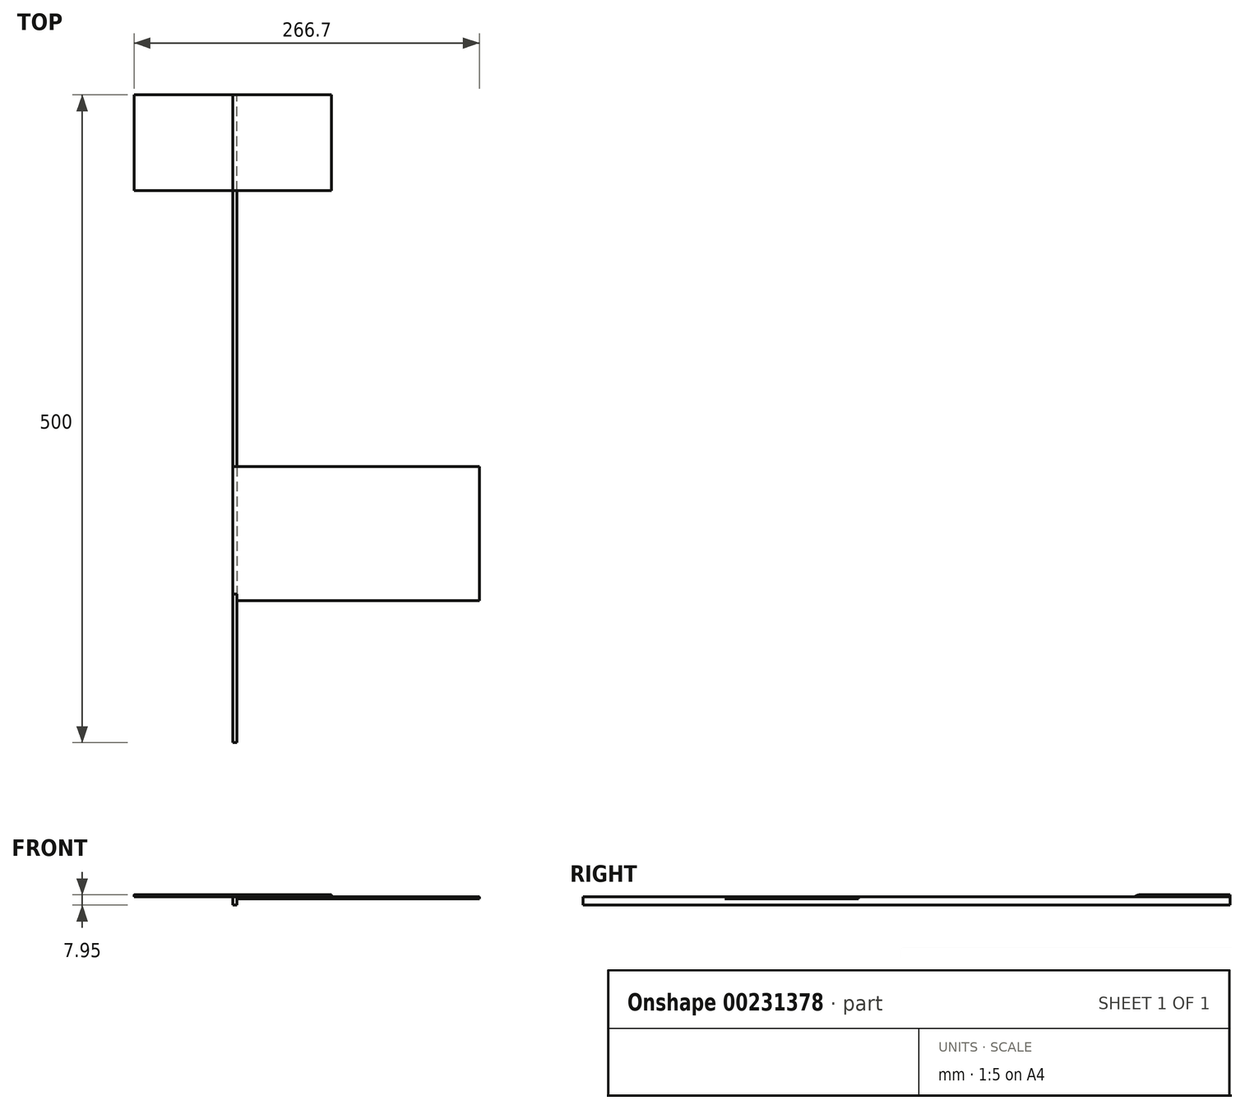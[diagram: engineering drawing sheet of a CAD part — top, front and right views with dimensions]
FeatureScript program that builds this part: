
annotation { "Feature Type Name" : "Feature", "Feature Type Description" : "" }
export const myFeature = defineFeature(function(context is Context, id is Id, definition is map)
    precondition{}
    {
        {
            var Q0;
            Q0=qCreatedBy(makeId("Front.planeOp"),FACE);
            var sketch = newSketch(context, id + "F0", { "sketchPlane" : qUnion([Q0])});
            skLineSegment(sketch, "E0.bottom", {"start": v(0, 0) * mm, "end": v(3.18, 0) * mm});
            skLineSegment(sketch, "E0.top", {"start": v(0, 6.35) * mm, "end": v(3.17, 6.35) * mm});
            skLineSegment(sketch, "E0.left", {"start": v(0, 0) * mm, "end": v(0, 6.35) * mm});
            skLineSegment(sketch, "E0.right", {"start": v(3.18, 0) * mm, "end": v(3.17, 6.35) * mm});
            skSolve(sketch);
        }
        {
            var Q0;
            Q0 = qSketchRegion(id + "F0", true);
            extrude(context, id + "F1", {"entities" : qUnion([Q0]), "depth" : 500 * mm});
        }
        {
            var Q0;
            Q0=qCreatedBy(makeId("Right.planeOp"),FACE);
            var sketch = newSketch(context, id + "F2", { "sketchPlane" : qUnion([Q0])});
            skLineSegment(sketch, "E1.bottom", {"start": v(0, 0) * mm, "end": v(-76.2, 0) * mm});
            skLineSegment(sketch, "E1.top", {"start": v(0, 7.95) * mm, "end": v(-69.85, 7.95) * mm});
            skLineSegment(sketch, "E1.left", {"start": v(0, 6.45) * mm, "end": v(0, 7.95) * mm});
            skLineSegment(sketch, "E1.right", {"start": v(-76.2, 0) * mm, "end": v(-76.2, 0.25) * mm});
            skPoint(sketch, "E2.visualSharp", {"position": v(-76.2, 7.95) * mm});
            skLineSegment(sketch, "E3.right", {"start": v(-76.2, 0) * mm, "end": v(-76.2, 1.6) * mm});
            skPoint(sketch, "E4", {"position": v(-76.2, 5.13) * mm});
            skArc(sketch, "E5.filletArc", {"start": v(-69.85, 7.95) * mm, "mid": v(-72.03, 7.56) * mm, "end": v(-73.95, 6.45) * mm});
            skPoint(sketch, "E6", {"position": v(-74.34, 6.1) * mm});
            skPoint(sketch, "E7", {"position": v(0, 6.45) * mm});
            skPoint(sketch, "E8", {"position": v(-73.95, 6.45) * mm});
            skLineSegment(sketch, "E9", {"start": v(0, 6.45) * mm, "end": v(-73.95, 6.45) * mm});
            skSolve(sketch);
        }
        {
            var Q0;
            Q0=makeQuery(id+"F2.imprint","IMPRINT",FACE,{"disambiguationData":[TD([[makeQuery(id+"F2.imprint","IMPRINT",EDGE,{"derivedFrom":sQuery(id+"F2.wireOp",EDGE,"E1.top")}),1.0]])]});
            extrude(context, id + "F3", {"entities" : qUnion([Q0]), "depth" : 76.2 * mm});
        }
        {
            var Q0;
            Q0=makeQuery(id+"F3.opExtrude","SWEPT_BODY",BODY,{"disambiguationData":[OSD([sQuery(id+"F2.wireOp",EDGE,"E1.top"),sQuery(id+"F2.wireOp",EDGE,"E1.left"),sQuery(id+"F2.wireOp",EDGE,"E5.filletArc"),sQuery(id+"F2.wireOp",EDGE,"E9")])]});
            var Q1;
            Q1=qCreatedBy(makeId("Right.planeOp"),FACE);
            mirror(context, id + "F4", {"operationType" : NewBodyOperationType.ADD, "entities" : qUnion([Q0]), "mirrorPlane" : qUnion([Q1])});
        }
        {
            var Q0;
            Q0=qCreatedBy(makeId("Right.planeOp"),FACE);
            var sketch = newSketch(context, id + "F5", { "sketchPlane" : qUnion([Q0])});
            skLineSegment(sketch, "E10.bottom", {"start": v(-287.02, 4.8) * mm, "end": v(-390.3, 4.8) * mm});
            skLineSegment(sketch, "E10.top", {"start": v(-287.02, 6.4) * mm, "end": v(-384.13, 6.4) * mm});
            skLineSegment(sketch, "E10.left", {"start": v(-287.02, 4.8) * mm, "end": v(-287.02, 6.4) * mm});
            skPoint(sketch, "E11.visualSharp", {"position": v(-396.83, 6.4) * mm});
            skArc(sketch, "E11.filletArc", {"start": v(-384.13, 6.4) * mm, "mid": v(-387.32, 5.99) * mm, "end": v(-390.3, 4.8) * mm});
            skSolve(sketch);
        }
        {
            var Q0;
            Q0=makeQuery(id+"F5.imprint","IMPRINT",FACE,{"disambiguationData":[TD([[makeQuery(id+"F5.imprint","IMPRINT",EDGE,{"derivedFrom":sQuery(id+"F5.wireOp",EDGE,"E10.bottom")}),-1.0]])]});
            extrude(context, id + "F6", {"entities" : qUnion([Q0]), "operationType" : NewBodyOperationType.ADD, "depth" : 190.5 * mm});
        }
    });
